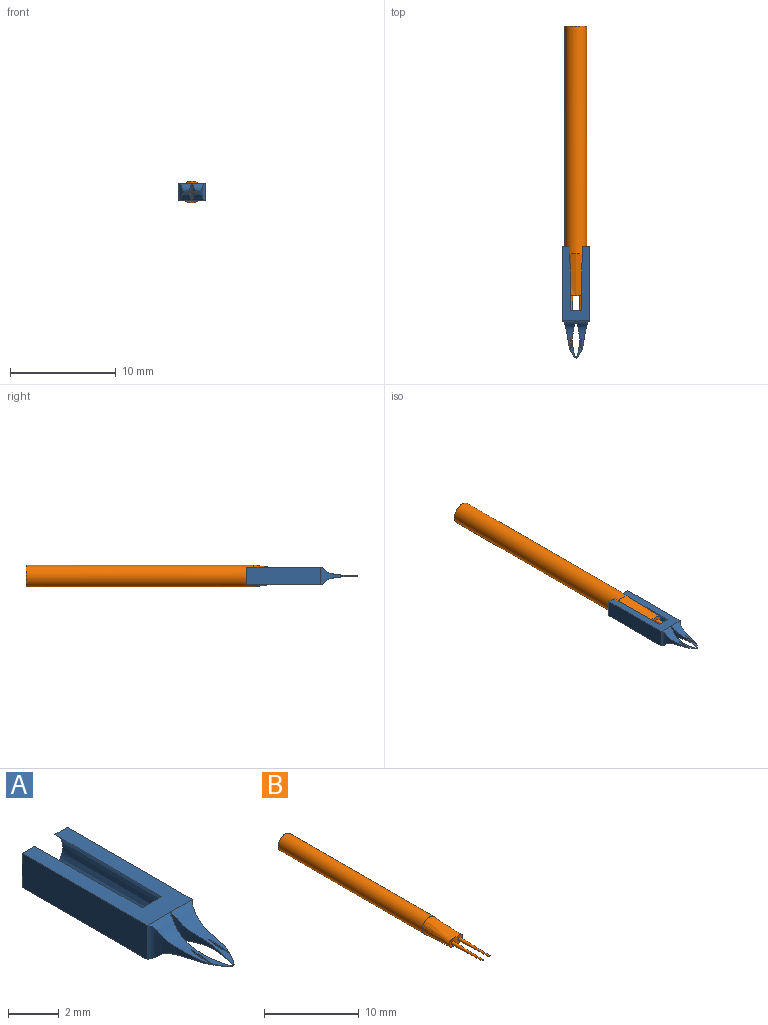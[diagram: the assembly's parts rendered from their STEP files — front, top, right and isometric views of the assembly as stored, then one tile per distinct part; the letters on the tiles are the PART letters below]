
ASSEMBLY  parts=2 mates=1
PART A: 47 faces, bbox 2.5x10.5x1.7 mm
  f0: plane 7.01x0.74mm, normal (0,0,-1), area 5mm2, adj f1,f43,f44,f45,f46
  f1: plane 1.65x0.69mm, normal (0,1,0), area 0.6mm2, adj f0,f2,f43,f46
  f2: plane 7x2.53mm, normal (0,0,1), area 11mm2, adj f1,f3,f38,f39,f40,f41,f42,f43
  f3: extruded ~3.52x1.26mm, area 1.9mm2, adj f2,f4,f29,f30,f31,f32,f33,f34
  f4: cylinder r=0mm len=0.02mm, axis (-1,0,0), area 0mm2, adj f3,f5,f29,f37
  f5: cylinder r=0mm len=0.02mm, axis (-1,0,0), area 0mm2, adj f4,f6,f28,f37
  f6: extruded ~3.52x1.27mm, area 1.9mm2, adj f5,f7,f27,f28,f30,f31,f32,f34
  f7: extruded ~0.05x0.02mm, area 0mm2, adj f6,f8,f32
  f8: plane 0.05x0.04mm, normal (0,0,-1), area 0mm2, adj f7,f9,f26,f32
  f9: plane 1.65x0.02mm, normal (0.73,-0.69,0), area 0mm2, adj f8,f10,f11,f12,f26,f32,f38,f44
  f10: extruded ~0.05x0.02mm, area 0mm2, adj f9,f11,f38
  f11: plane 0.05x0.04mm, normal (0,0,1), area 0mm2, adj f9,f10,f32,f33
  f12: cylinder r=0.01mm len=1.61mm, axis (0,0,1), area 0mm2, adj f9,f13,f38,f44
  f13: extruded ~3.42x1.6mm, area 1.3mm2, adj f12,f14,f38,f44
  f14: bspline ~0.04x0.02mm, area 0mm2, adj f13,f15,f17,f25
  f15: cylinder r=0mm len=0.02mm, axis (1,0,0), area 0mm2, adj f14,f16,f17,f25,f28,f29
  f16: bspline ~0.04x0.02mm, area 0mm2, adj f15,f28,f29,f30
  f17: bspline ~0.04x0.02mm, area 0mm2, adj f14,f15,f18,f25,f38
  f18: cylinder r=0mm len=0.02mm, axis (1,0,0), area 0mm2, adj f17,f19,f24,f38
  f19: extruded ~0.62x0.44mm, area 0mm2, adj f18,f20,f24,f38,f44
  f20: cone r=0.23mm half-angle=4.1deg, axis (0,1,0), area 2.1mm2, adj f19,f21,f22,f23,f38,f44
  f21: cylinder r=0.23mm len=1mm, axis (0,-1,0), area 1.4mm2, adj f20,f39
  f22: cone r=0.23mm half-angle=4.1deg, axis (0,1,0), area 0mm2, adj f20,f44
  f23: extruded ~2.84x1.65mm, area 1.5mm2, adj f20,f38,f43,f44
  f24: cylinder r=0mm len=0.02mm, axis (1,0,0), area 0mm2, adj f18,f19,f25,f44
  f25: bspline ~0.04x0.02mm, area 0mm2, adj f14,f15,f17,f24,f44
  f26: extruded ~0.05x0.02mm, area 0mm2, adj f8,f9,f44
  f27: plane 7.01x0.74mm, normal (0,0,-1), area 5mm2, adj f6,f40,f41,f42,f45
  f28: bspline ~0.04x0.02mm, area 0mm2, adj f5,f6,f15,f16,f29
  f29: bspline ~0.04x0.02mm, area 0mm2, adj f3,f4,f15,f16,f28
  f30: extruded ~3.42x1.6mm, area 1.3mm2, adj f3,f6,f16,f31
  f31: cylinder r=0.01mm len=1.61mm, axis (0,0,1), area 0mm2, adj f3,f6,f30,f32
  f32: plane 1.65x0.02mm, normal (-0.73,-0.69,0), area 0mm2, adj f3,f6,f7,f8,f9,f11,f31,f33
  f33: extruded ~0.05x0.02mm, area 0mm2, adj f3,f11,f32
  f34: extruded ~2.84x1.65mm, area 1.5mm2, adj f3,f6,f35,f42
  f35: cone r=0.23mm half-angle=4.1deg, axis (0,1,0), area 2.2mm2, adj f3,f6,f34,f36,f37
  f36: cylinder r=0.23mm len=1mm, axis (0,-1,0), area 1.4mm2, adj f35,f39
  f37: extruded ~0.62x0.44mm, area 0mm2, adj f3,f4,f5,f6,f35
  f38: extruded ~3.52x1.26mm, area 1.9mm2, adj f2,f9,f10,f12,f13,f17,f18,f19
  f39: plane 1.97x1.65mm, normal (0,1,0), area 2.5mm2, adj f2,f21,f36,f40,f45,f46
  f40: cone r=1.01mm half-angle=0.2deg, axis (0,1,0), area 11.6mm2, adj f2,f27,f39,f41
  f41: plane 1.65x0.69mm, normal (0,1,0), area 0.6mm2, adj f2,f27,f40,f42
  f42: plane 7x1.65mm, normal (1,0,0), area 11.5mm2, adj f2,f27,f34,f41
  f43: plane 7x1.65mm, normal (-1,0,0), area 11.5mm2, adj f0,f1,f2,f23
  f44: extruded ~3.52x1.26mm, area 1.9mm2, adj f0,f9,f12,f13,f19,f20,f22,f23
  f45: plane 1.1x1.01mm, normal (0,0,-1), area 1.1mm2, adj f0,f6,f27,f39,f44
  f46: cone r=1.01mm half-angle=0.2deg, axis (0,1,0), area 11.6mm2, adj f0,f1,f2,f39
PART B: 8 faces, bbox 2.1x30.1x2.1 mm
  f0: cone r=0.21mm half-angle=1.7deg, axis (0,1,0), area 4.1mm2, adj f1,f4
  f1: plane 0.16x0.16mm, normal (0,-1,0), area 0mm2, adj f0
  f2: cylinder r=1.04mm len=21.55mm, axis (0,-1,0), area 140.3mm2, adj f3,f5
  f3: plane 2.07x2.07mm, normal (0,1,0), area 3.4mm2, adj f2
  f4: plane 2.07x1.02mm, normal (0,-1,0), area 1.6mm2, adj f0,f5,f6
  f5: bspline ~4x2.07mm, area 23.2mm2, adj f2,f4
  f6: cone r=0.21mm half-angle=1.7deg, axis (0,1,0), area 4.1mm2, adj f4,f7
  f7: plane 0.16x0.16mm, normal (0,-1,0), area 0mm2, adj f6
PLACE A t=(-3.98,-0.87,-3.78)mm
PLACE B t=(-3.99,5.01,-3.78)mm
MATE slider B.f0 <-> A.f35  axis (0,-1,0) through (-3.48,0.51,-3.78)mm
